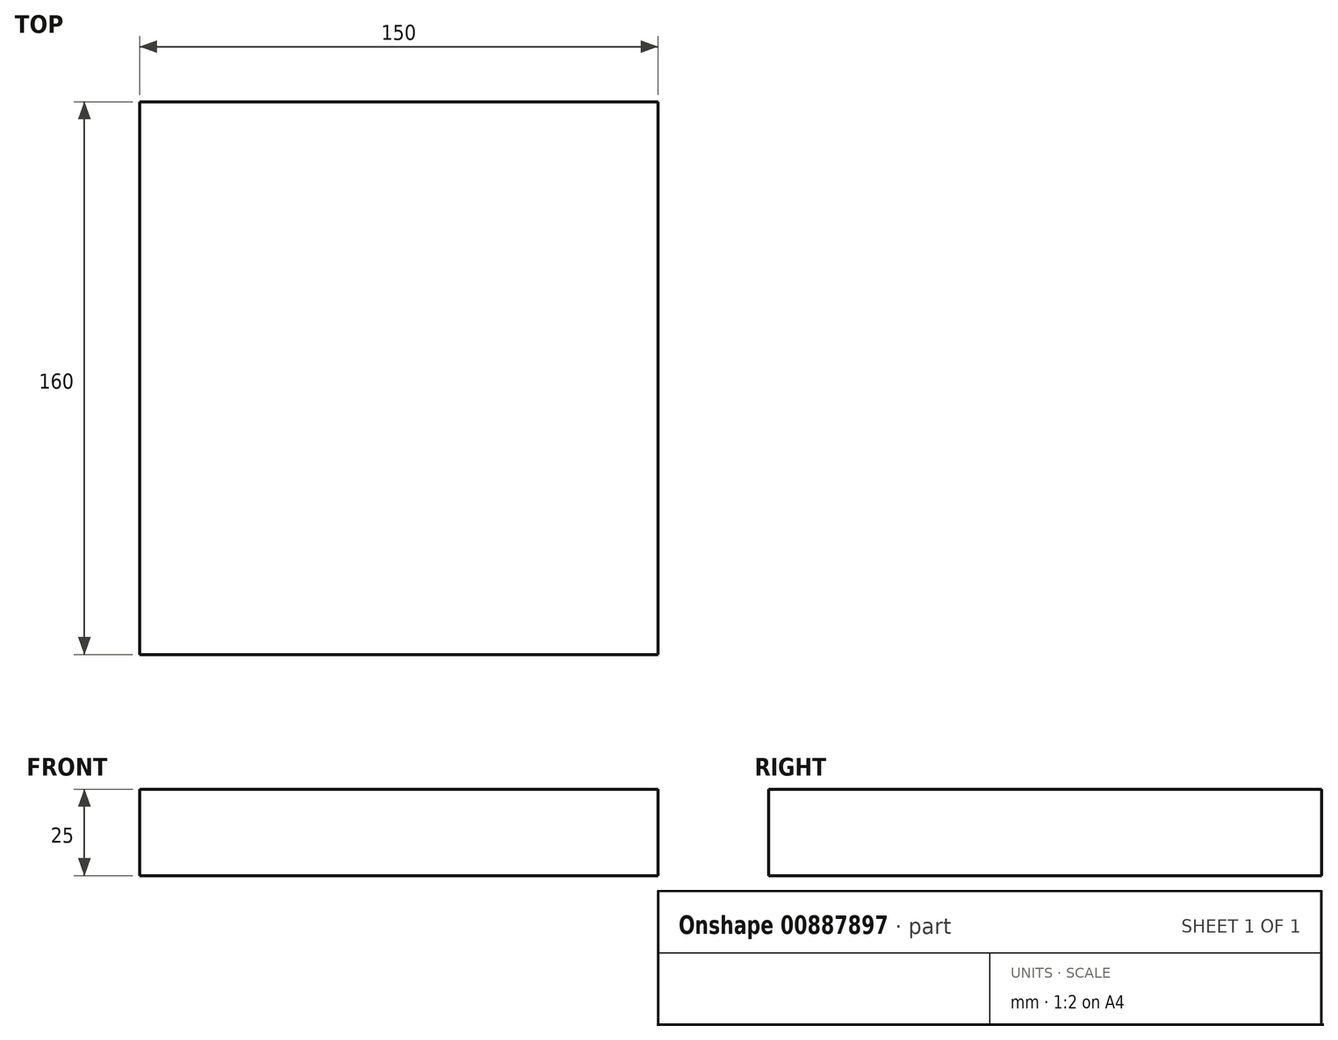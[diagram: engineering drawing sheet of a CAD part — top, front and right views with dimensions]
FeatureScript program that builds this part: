
annotation { "Feature Type Name" : "Feature", "Feature Type Description" : "" }
export const myFeature = defineFeature(function(context is Context, id is Id, definition is map)
    precondition{}
    {
        {
            var Q0;
            Q0=qCreatedBy(makeId("Top.planeOp"),FACE);
            var sketch = newSketch(context, id + "F0", { "sketchPlane" : qUnion([Q0])});
            skLineSegment(sketch, "E0.bottom", {"start": v(-75, 80) * mm, "end": v(75, 80) * mm});
            skLineSegment(sketch, "E0.top", {"start": v(-75, -80) * mm, "end": v(75, -80) * mm});
            skLineSegment(sketch, "E0.left", {"start": v(-75, 80) * mm, "end": v(-75, -80) * mm});
            skLineSegment(sketch, "E0.right", {"start": v(75, 80) * mm, "end": v(75, -80) * mm});
            skPoint(sketch, "E0.middle", {"position": v(0, 0) * mm});
            skSolve(sketch);
        }
        {
            var Q0;
            Q0=makeQuery(id+"F0.imprint","IMPRINT",FACE,{"disambiguationData":[TD([[makeQuery(id+"F0.imprint","IMPRINT",EDGE,{"derivedFrom":sQuery(id+"F0.wireOp",EDGE,"E0.bottom")}),-1.0]])]});
            extrude(context, id + "F1", {"entities" : qUnion([Q0]), "depth" : 25 * mm, "offsetDistance" : 25 * mm});
        }
    });
